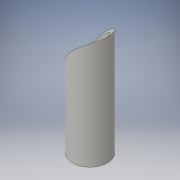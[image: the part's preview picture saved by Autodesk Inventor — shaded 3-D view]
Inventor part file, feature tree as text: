
AUTODESK INVENTOR PART (.ipt)
format: ipt  version: 2016 (Build 200138000, 138)  size: 130,048 bytes
history: native  units: in
note: dims shown in document units (in); Inventor stores cm internally (conversion verified against a paired STEP export)
features: extrude x5, sketch x5, plane x4
ambient origin geometry x8: Origin, YZ Plane, XZ Plane, XY Plane, X Axis, Y Axis, Z Axis, Center Point
bodies: Solid1 (feature_tree)
feature tree (14):
  extrude  "Extrusion1"  Depth=1.913in
  plane  "Work Plane4"
  extrude  "Extrusion2"  Depth=3.0in
  extrude  "Extrusion3"  Depth=2.248in
  extrude  "Extrusion4"  Depth=2.248in
  extrude  "Extrusion5"  Depth=0.5in TaperAngle=0.0deg
  sketch  "Sketch1"  dims[d0=1.58in d1=1.913in]
  plane  "Work Plane1"
  plane  "Work Plane2"
  plane  "Work Plane3"
  sketch  "Sketch2"  dims[d2=6.0in d3=0.0in d4=3.0in]
  sketch  "Sketch3"  dims[d5=0.84in d6=2.248in]
  sketch  "Sketch4"  dims[d7=2.248in d8=4.496in]
  sketch  "Sketch5"  dims[d9=6.0in d10=0.0in d11=2.5in d12=0.0in d13=2.0in d14=0.0in d15=0.5in d16=0.0in]
